# Revit family: Electronics_Visual-Projectors_ViewSonic_The-ViewSonicR-PRO8530HDL-Projector
name_source: partatom
category: Electrical Equipment
revit_build: Autodesk Revit 2015 (Build: 20140606_1530(x64)
units: mm (PartAtom-declared; Revit-internal decimal feet)

## types (1)
- PRO8530HDL
    Assembly Code = D50
    BIMobject category = Visual - Projectors
    BIMobject category code = electronics-visual-projectors
    BIMobject main category = Electronics
    BIMobject main category code = electronics
    BOSUseNativeGeometries = 1
    Brand url = https://www.viewsonic.com
    Covering Color = Plastic - Viewsonic - White
    Description = The Pro8530HDL is the perfect solution for large venue Pro AV projection requirements, thanks to a centred lens, sealed engine and multiple adjustment features like vertical lens shift, 1.6x optical zoom, horizontal & vertical keystone, plus 4-corner adjustment. Utilising a unique "Flex-In" (Flexible Installation) design, the Pro8530HDL integrates an intuitive form with high flexibility and an easy installation process, making it the ideal installation projector. Equipped with 5,200 lumens and Full HD resolution, the Pro8530HDL is powered by SuperColor™ and SonicExpert® to provide a professional audiovisual performance. It boasts a bilateral opening top cover, 4x HDMI (1 of which is MHL) and an intuitive PortAll® compartment to accommodate optinal HDBaseT solutions (an affordable way of transferring High Definition audio and video over long distance), wireless dongles, or PC stick integration for versatile application.
    Design country = Taiwan
    Edition number = 1
    Keynote = V90
    Manufacturer = ViewSonic
    Manufacturer country = Taiwan
    Manufacturer name = ViewSonic
    Model = viewsonic_8530 hdl
    Product Guid = a843d93d-3c96-4c77-a81f-4db7443d46a7
    Product SKU = viewsonic_PRO8530HDL
    Product data url = https://bimobject.com
    Product family = Electronics
    Product group = Projectors
    Product name = The ViewSonic® PRO8530HDL Projector
    Product url = https://www.viewsonic.com
    QR code = http://bimobject.com
    URL = www.viewsonic.com
    a = Image Aspect Ratio : "4  - 3"
    b = Image Aspect Ratio : "16 - 9"
    c = Image Aspect Ratio : "16 - 10"

## geometry (parser evidence)
native form markers: Blend x2, Sweep x7
no freeform markers — native parametric forms only
